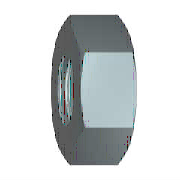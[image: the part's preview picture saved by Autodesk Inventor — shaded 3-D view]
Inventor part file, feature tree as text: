
AUTODESK INVENTOR PART (.ipt)
format: ipt  version: 2021 (Build 250183000, 183)  size: 164,864 bytes
history: native  units: mm (DEFAULTED — no unit token found)
features: sketch x3, chamfer x1, hole x1, other x1, plane x1
ambient origin geometry x7: Origin, YZ Plane, XZ Plane, X Axis, Y Axis, Z Axis, Center Point
bodies: Solid1 (feature_tree), Body (feature_tree)
feature tree (7):
  chamfer  "Chamfer1"  Angle=30.0deg  [1 undecoded]
  hole  "Thread"  [1 undecoded]
  other  "Work Axis1"
  plane  "Work Plane1"
  sketch  "Sketch1"  dims[d0=27.712813mm]
  sketch  "Sketch2"  dims[d1=14.8mm]
  sketch  "Sketch3"  dims[d2=0.0mm d3=30.0deg d4=30.0deg d5=22.5mm d6=22.5mm d7=90.0deg d25=13.835mm d26=6.0mm d27=4.0mm d28=2.0mm d29=14.3117mm d30=8.0mm d31=20.594885mm d8=1.082532mm d9=30.0deg d10=1.082532mm d11=30.0deg d13=0.0mm d14=0.0mm d39=0.0mm d40=1.082532mm d41=1.082532mm d42=0.0mm]
note: 2 required parameter values undecoded (feature->parameter linkage not recoverable at this tier; creation-order binding heuristic only, values carry confidence <= 0.55)
